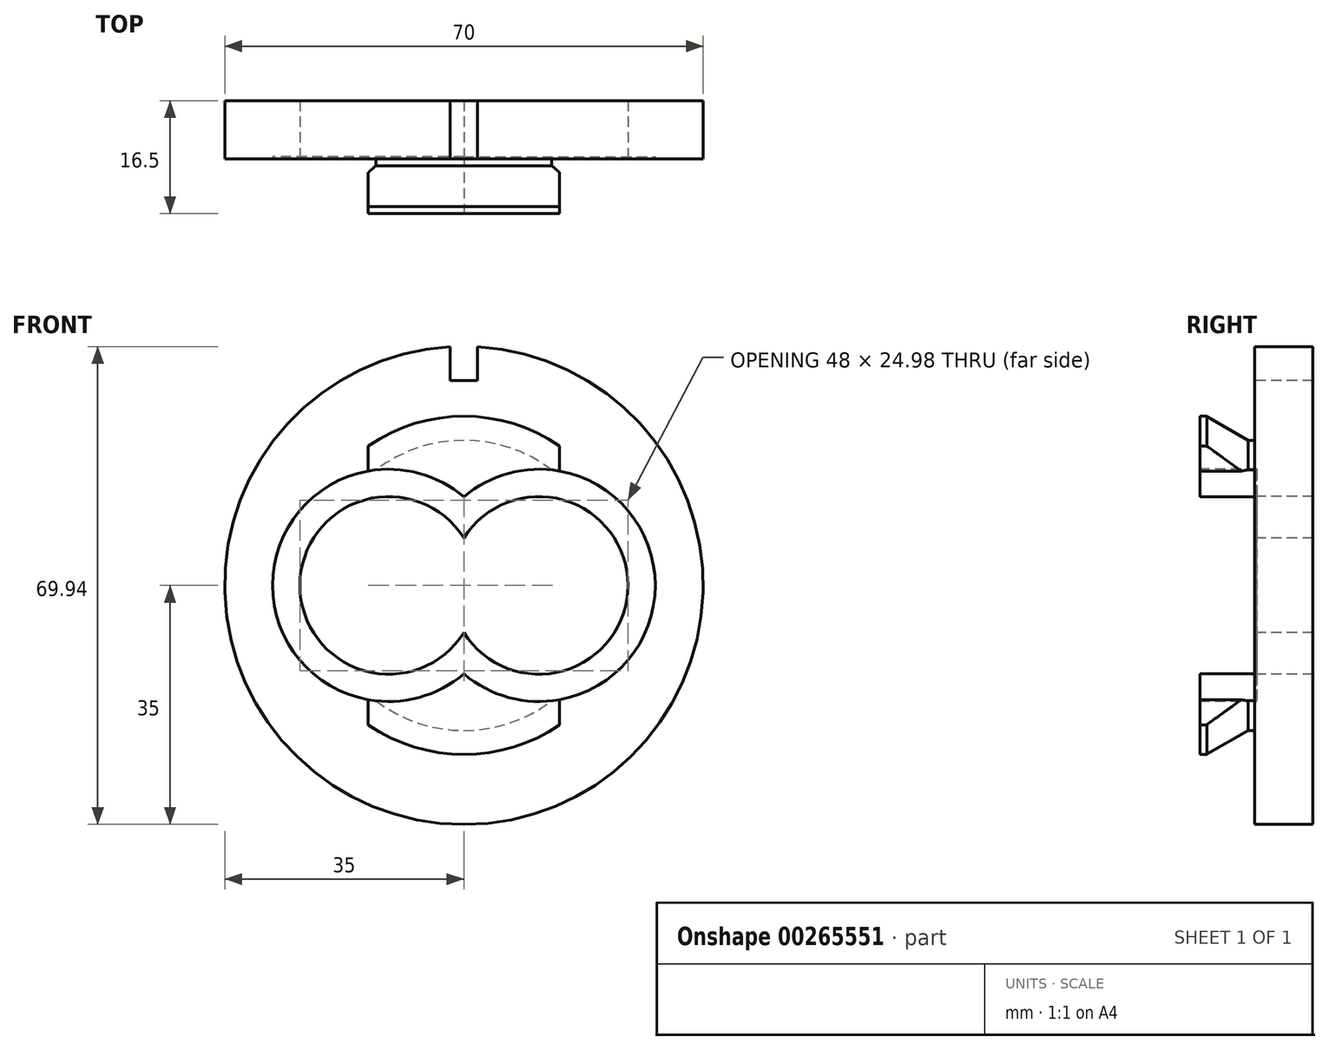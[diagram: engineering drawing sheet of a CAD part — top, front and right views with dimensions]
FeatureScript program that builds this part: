
annotation { "Feature Type Name" : "Feature", "Feature Type Description" : "" }
export const myFeature = defineFeature(function(context is Context, id is Id, definition is map)
    precondition{}
    {
        {
            var Q0;
            Q0=qCreatedBy(makeId("Front.planeOp"),FACE);
            var sketch = newSketch(context, id + "F0", { "sketchPlane" : qUnion([Q0])});
            skCircle(sketch, "E0", {"center": v(0, 0) * mm, "radius": 35 * mm});
            skSolve(sketch);
        }
        {
            var Q0;
            Q0 = qSketchRegion(id + "F0", true);
            extrude(context, id + "F1", {"entities" : qUnion([Q0]), "depth" : 8.5 * mm});
        }
        {
            var Q0;
            Q0=makeQuery(id+"F1.opExtrude","CAP_FACE",FACE,{"disambiguationData":[OSD([sQuery(id+"F0.wireOp",EDGE,"E0")])],"isStart":false});
            var sketch = newSketch(context, id + "F2", { "sketchPlane" : qUnion([Q0])});
            skCircle(sketch, "E1", {"center": v(0, 0) * mm, "radius": 21.24 * mm});
            skSolve(sketch);
        }
        {
            var Q0;
            Q0 = qSketchRegion(id + "F2", true);
            extrude(context, id + "F3", {"entities" : qUnion([Q0]), "operationType" : NewBodyOperationType.ADD, "depth" : 1 * mm});
        }
        {
            var Q0;
            Q0=makeQuery(id+"F3.opExtrude","CAP_FACE",FACE,{"disambiguationData":[OSD([sQuery(id+"F2.wireOp",EDGE,"E1")])],"isStart":false});
            var sketch = newSketch(context, id + "F4", { "sketchPlane" : qUnion([Q0])});
            skCircle(sketch, "E2", {"center": v(0, 0) * mm, "radius": 21.24 * mm});
            skSolve(sketch);
        }
        {
            var Q0;
            Q0 = qSketchRegion(id + "F4", true);
            extrude(context, id + "F5", {"entities" : qUnion([Q0]), "operationType" : NewBodyOperationType.ADD, "depth" : 6 * mm, "hasDraft" : true, "draftAngle" : 30 * degree});
        }
        {
            var Q0;
            Q0=makeQuery(id+"F5.opExtrude","CAP_FACE",FACE,{"disambiguationData":[OSD([sQuery(id+"F4.wireOp",EDGE,"E2")])],"isStart":false});
            var sketch = newSketch(context, id + "F6", { "sketchPlane" : qUnion([Q0])});
            skCircle(sketch, "E3", {"center": v(0, 0) * mm, "radius": 24.75 * mm});
            skSolve(sketch);
        }
        {
            var Q0;
            Q0 = qSketchRegion(id + "F6", true);
            extrude(context, id + "F7", {"entities" : qUnion([Q0]), "operationType" : NewBodyOperationType.ADD, "depth" : 1 * mm});
        }
        {
            var Q0;
            Q0=makeQuery(id+"F7.opExtrude","CAP_FACE",FACE,{"disambiguationData":[OSD([sQuery(id+"F6.wireOp",EDGE,"E3")])],"isStart":false});
            var sketch = newSketch(context, id + "F8", { "sketchPlane" : qUnion([Q0])});
            skCircle(sketch, "E4", {"center": v(-11, 0) * mm, "radius": 13 * mm});
            skCircle(sketch, "E5", {"center": v(11, 0) * mm, "radius": 13 * mm});
            skSolve(sketch);
        }
        {
            var Q0;
            Q0 = qSketchRegion(id + "F8", true);
            extrude(context, id + "F9", {"entities" : qUnion([Q0]), "operationType" : NewBodyOperationType.REMOVE, "oppositeDirection" : true, "depth" : 16.5 * mm});
        }
        {
            var Q0;
            Q0=makeQuery(id+"F7.opExtrude","CAP_FACE",FACE,{"disambiguationData":[OSD([sQuery(id+"F6.wireOp",EDGE,"E3")])],"isStart":false});
            var sketch = newSketch(context, id + "F10", { "sketchPlane" : qUnion([Q0])});
            skCircle(sketch, "E6", {"center": v(-11, 0) * mm, "radius": 17 * mm});
            skCircle(sketch, "E7", {"center": v(11, 0) * mm, "radius": 17 * mm});
            skSolve(sketch);
        }
        {
            var Q0;
            Q0 = qSketchRegion(id + "F10", true);
            extrude(context, id + "F11", {"entities" : qUnion([Q0]), "operationType" : NewBodyOperationType.REMOVE, "oppositeDirection" : true, "depth" : 8.3 * mm});
        }
        {
            var Q0;
            Q0=makeQuery(id+"F11.boolean.opBoolean","SPLIT",FACE,{"disambiguationData":[OD(0.0)],"derivedFrom":makeQuery(id+"F7.opExtrude","CAP_FACE",FACE,{"disambiguationData":[OSD([sQuery(id+"F6.wireOp",EDGE,"E3")])],"isStart":false})});
            var sketch = newSketch(context, id + "F12", { "sketchPlane" : qUnion([Q0])});
            skLineSegment(sketch, "E8.bottom", {"start": v(14, 26.75) * mm, "end": v(26.05, 26.75) * mm});
            skLineSegment(sketch, "E8.top", {"start": v(14, -25.44) * mm, "end": v(26.05, -25.44) * mm});
            skLineSegment(sketch, "E8.left", {"start": v(14, 26.75) * mm, "end": v(14, -25.44) * mm});
            skLineSegment(sketch, "E8.right", {"start": v(26.05, 26.75) * mm, "end": v(26.05, -25.44) * mm});
            skLineSegment(sketch, "E9.bottom", {"start": v(-14, 28.66) * mm, "end": v(-24.44, 28.66) * mm});
            skLineSegment(sketch, "E9.top", {"start": v(-14, -24.11) * mm, "end": v(-24.44, -24.11) * mm});
            skLineSegment(sketch, "E9.left", {"start": v(-14, 28.66) * mm, "end": v(-14, -24.11) * mm});
            skLineSegment(sketch, "E9.right", {"start": v(-24.44, 28.66) * mm, "end": v(-24.44, -24.11) * mm});
            skSolve(sketch);
        }
        {
            var Q0;
            Q0 = qSketchRegion(id + "F12", true);
            extrude(context, id + "F13", {"entities" : qUnion([Q0]), "operationType" : NewBodyOperationType.REMOVE, "oppositeDirection" : true, "depth" : 8 * mm});
        }
        {
            var Q0;
            Q0=makeQuery(id+"F1.opExtrude","CAP_FACE",FACE,{"disambiguationData":[OSD([sQuery(id+"F0.wireOp",EDGE,"E0")])],"isStart":false});
            var sketch = newSketch(context, id + "F14", { "sketchPlane" : qUnion([Q0])});
            skLineSegment(sketch, "E10.bottom", {"start": v(-2, 36) * mm, "end": v(2, 36) * mm});
            skLineSegment(sketch, "E10.top", {"start": v(-2, 30) * mm, "end": v(2, 30) * mm});
            skLineSegment(sketch, "E10.left", {"start": v(-2, 36) * mm, "end": v(-2, 30) * mm});
            skLineSegment(sketch, "E10.right", {"start": v(2, 36) * mm, "end": v(2, 30) * mm});
            skSolve(sketch);
        }
        {
            var Q0;
            Q0 = qSketchRegion(id + "F14", true);
            extrude(context, id + "F15", {"entities" : qUnion([Q0]), "operationType" : NewBodyOperationType.REMOVE, "oppositeDirection" : true, "depth" : 8.5 * mm});
        }
    });
